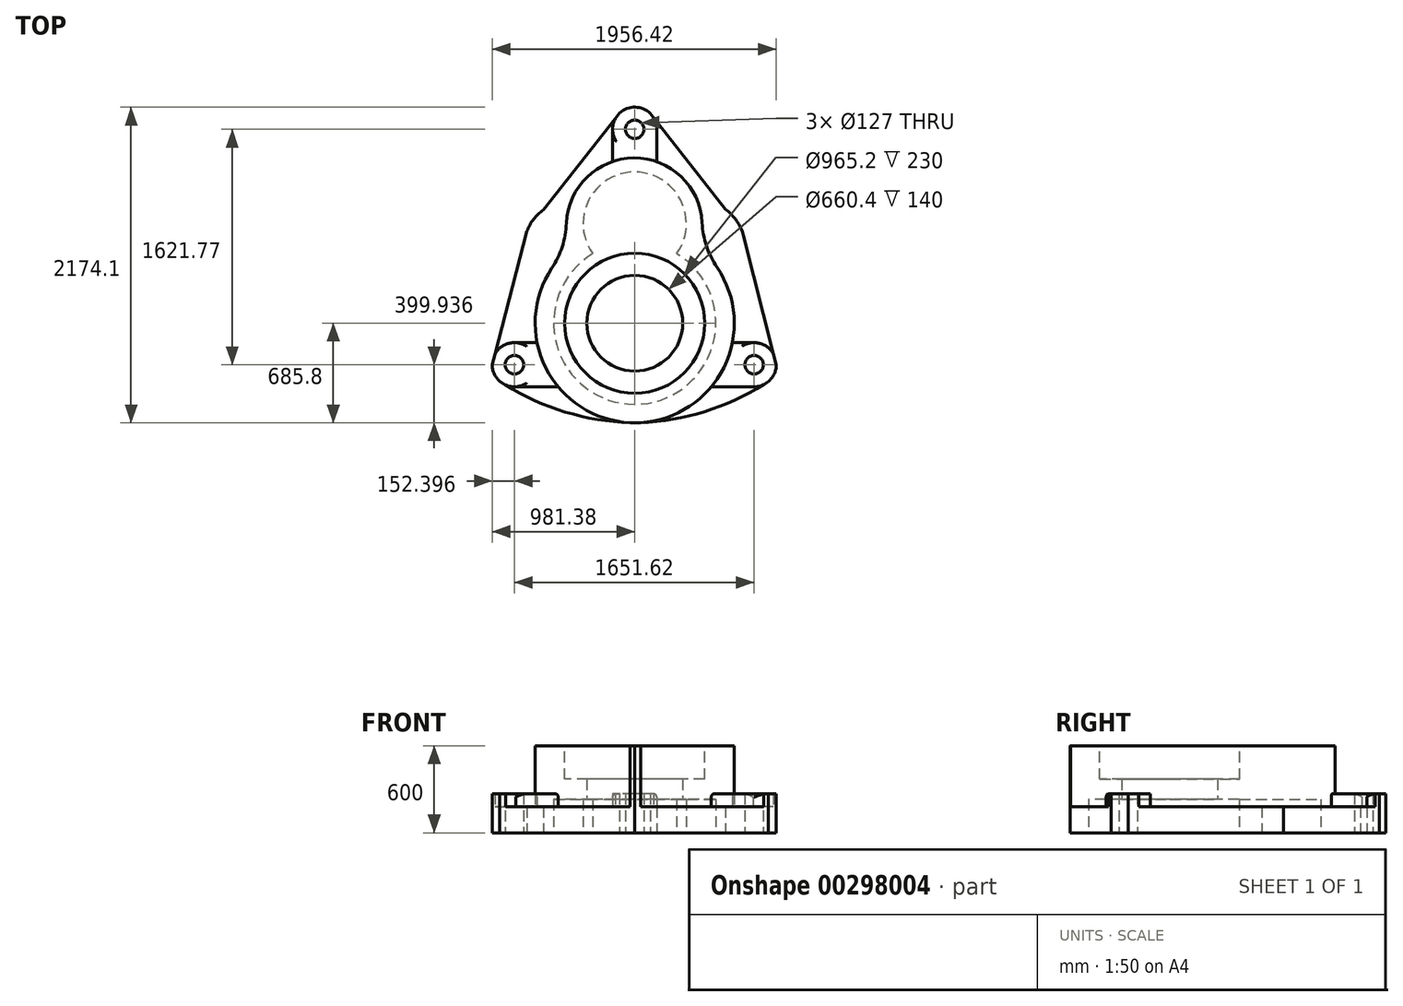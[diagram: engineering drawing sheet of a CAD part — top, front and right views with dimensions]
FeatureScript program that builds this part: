
annotation { "Feature Type Name" : "Feature", "Feature Type Description" : "" }
export const myFeature = defineFeature(function(context is Context, id is Id, definition is map)
    precondition{}
    {
        {
            var Q0;
            Q0=qCreatedBy(makeId("Top.planeOp"),FACE);
            var sketch = newSketch(context, id + "F0", { "sketchPlane" : qUnion([Q0])});
            skArc(sketch, "E0", {"start": v(-446.41, 520.61) * mm, "mid": v(3.07, -685.8) * mm, "end": v(441.73, 524.6) * mm});
            skCircle(sketch, "E1", {"center": v(0, 0) * mm, "radius": 330.2 * mm});
            skCircle(sketch, "E2", {"center": v(0, 0) * mm, "radius": 558.8 * mm});
            skCircle(sketch, "E3", {"center": v(-828.98, -285.86) * mm, "radius": 152.4 * mm});
            skCircle(sketch, "E4", {"center": v(822.64, -285.7) * mm, "radius": 152.4 * mm});
            skCircle(sketch, "E5", {"center": v(-828.98, -285.86) * mm, "radius": 63.5 * mm});
            skCircle(sketch, "E6", {"center": v(822.64, -285.7) * mm, "radius": 63.5 * mm});
            skLineSegment(sketch, "E7", {"start": v(-819.33, -437.96) * mm, "end": v(-527.72, -437.98) * mm});
            skLineSegment(sketch, "E8", {"start": v(-828.61, -133.46) * mm, "end": v(-672.69, -133.46) * mm});
            skLineSegment(sketch, "E9.trimOffspring", {"start": v(672.69, -133.46) * mm, "end": v(815.7, -133.46) * mm});
            skLineSegment(sketch, "E10.trimOffspring", {"start": v(527.64, -438.08) * mm, "end": v(822.62, -438.1) * mm});
            skCircle(sketch, "E11", {"center": v(0, 685.8) * mm, "radius": 355.6 * mm});
            skArc(sketch, "E12.trimOffspring", {"start": v(441.73, 524.6) * mm, "mid": v(-5.1, 1138.5) * mm, "end": v(-446.41, 520.61) * mm});
            skPoint(sketch, "E13.centerSnap0", {"position": v(-5.1, 1138.5) * mm});
            skArc(sketch, "E14", {"start": v(-132.99, 1410.33) * mm, "mid": v(2.72, 1183.53) * mm, "end": v(130.25, 1415.03) * mm});
            skLineSegment(sketch, "E15", {"start": v(150.95, 1356.87) * mm, "end": v(150.95, 1112.47) * mm});
            skLineSegment(sketch, "E16", {"start": v(-151.85, 1322.98) * mm, "end": v(-151.85, 1114.21) * mm});
            skCircle(sketch, "E17", {"center": v(0, 1335.9) * mm, "radius": 63.5 * mm});
            skLineSegment(sketch, "E18", {"start": v(-981.36, -283) * mm, "end": v(-981.36, -283) * mm});
            skArc(sketch, "E19", {"start": v(749.46, 602.73) * mm, "mid": v(702.96, 705.05) * mm, "end": v(623.72, 784.76) * mm});
            skArc(sketch, "E20", {"start": v(-628.54, 780.68) * mm, "mid": v(-717.12, 686.52) * mm, "end": v(-760.82, 564.85) * mm});
            skPoint(sketch, "E21.start.orphan", {"position": v(975.04, -285.7) * mm});
            skLineSegment(sketch, "E22", {"start": v(-981.36, -283) * mm, "end": v(-742.52, 635.17) * mm});
            skLineSegment(sketch, "E23", {"start": v(975.04, -285.7) * mm, "end": v(741.57, 633.83) * mm});
            skPoint(sketch, "E23.endSnap0", {"position": v(741.57, 629.01) * mm});
            skLineSegment(sketch, "E24", {"start": v(741.57, 633.83) * mm, "end": v(738.26, 638.07) * mm});
            skPoint(sketch, "E25.start.orphan", {"position": v(0, -685.8) * mm});
            skArc(sketch, "E26", {"start": v(-929.9, -400.07) * mm, "mid": v(-485.35, -609.35) * mm, "end": v(0, -685.8) * mm});
            skArc(sketch, "E27", {"start": v(0, -685.8) * mm, "mid": v(479.78, -609.45) * mm, "end": v(919.67, -403.23) * mm});
            skCircle(sketch, "E28", {"center": v(0, 0) * mm, "radius": 482.6 * mm});
            skArc(sketch, "E29.trimOffspring", {"start": v(343.44, 593.6) * mm, "mid": v(0, 685.8) * mm, "end": v(-343.44, 593.6) * mm});
            skLineSegment(sketch, "E30", {"start": v(130.25, 1415.03) * mm, "end": v(108.06, 1443.36) * mm});
            skLineSegment(sketch, "E31", {"start": v(-132.99, 1410.33) * mm, "end": v(-103.6, 1447.67) * mm});
            skArc(sketch, "E32.trimOffspring", {"start": v(108.06, 1443.36) * mm, "mid": v(3.1, 1488.27) * mm, "end": v(-103.6, 1447.67) * mm});
            skPoint(sketch, "E33", {"position": v(-110.4, 1439.03) * mm});
            skLineSegment(sketch, "E34", {"start": v(-628.54, 780.68) * mm, "end": v(-110.4, 1439.03) * mm});
            skPoint(sketch, "E35", {"position": v(111.45, 1439.03) * mm});
            skLineSegment(sketch, "E36", {"start": v(623.72, 784.76) * mm, "end": v(111.45, 1439.03) * mm});
            skSolve(sketch);
        }
        {
            var Q0;
            {var subQ6=sQuery(id+"F0.wireOp",EDGE,"E0");var subQ9=sQuery(id+"F0.wireOp",EDGE,"E12.trimOffspring");var subQ11=makeQuery(id+"F0.imprint","INTERSECT",VERTEX,{"disambiguationData":[OD(0.0)],"derivedFrom":[subQ6,subQ9]});Q0=makeQuery(id+"F0.imprint","IMPRINT",FACE,{"disambiguationData":[TD([[makeQuery(id+"F0.imprint","IMPRINT",EDGE,{"disambiguationData":[TD([[subQ11,-1.0]])],"derivedFrom":subQ6}),1.0]])]});}
            var Q1;
            {var subQ0=sQuery(id+"F0.wireOp",EDGE,"E29.trimOffspring");Q1=makeQuery(id+"F0.imprint","IMPRINT",FACE,{"disambiguationData":[TD([[makeQuery(id+"F0.imprint","IMPRINT",EDGE,{"derivedFrom":subQ0}),-1.0]])]});}
            var Q2;
            {var subQ4=sQuery(id+"F0.wireOp",EDGE,"E29.trimOffspring");Q2=makeQuery(id+"F0.imprint","IMPRINT",FACE,{"disambiguationData":[TD([[makeQuery(id+"F0.imprint","IMPRINT",EDGE,{"derivedFrom":subQ4}),1.0]])]});}
            var Q3;
            {var subQ0=sQuery(id+"F0.wireOp",EDGE,"E11");var subQ1=sQuery(id+"F0.wireOp",EDGE,"E2");var subQ2=makeQuery(id+"F0.imprint","INTERSECT",VERTEX,{"disambiguationData":[OD(0.0)],"derivedFrom":[subQ1,subQ0]});Q3=makeQuery(id+"F0.imprint","IMPRINT",FACE,{"disambiguationData":[TD([[makeQuery(id+"F0.imprint","IMPRINT",EDGE,{"disambiguationData":[TD([[subQ2,1.0]])],"derivedFrom":subQ1}),1.0]])]});}
            var Q4;
            {var subQ0=sQuery(id+"F0.wireOp",EDGE,"E11");var subQ1=makeQuery(id+"F0.imprint","INTERSECT",VERTEX,{"derivedFrom":[sQuery(id+"F0.wireOp",EDGE,"E1"),subQ0]});Q4=makeQuery(id+"F0.imprint","IMPRINT",FACE,{"disambiguationData":[TD([[makeQuery(id+"F0.imprint","IMPRINT",EDGE,{"disambiguationData":[TD([[subQ1,1.0]])],"derivedFrom":subQ0}),1.0]])]});}
            var Q5;
            {var subQ0=sQuery(id+"F0.wireOp",EDGE,"E11");var subQ1=sQuery(id+"F0.wireOp",EDGE,"E2");var subQ2=makeQuery(id+"F0.imprint","INTERSECT",VERTEX,{"disambiguationData":[OD(0.0)],"derivedFrom":[subQ1,subQ0]});Q5=makeQuery(id+"F0.imprint","IMPRINT",FACE,{"disambiguationData":[TD([[makeQuery(id+"F0.imprint","IMPRINT",EDGE,{"disambiguationData":[TD([[subQ2,-1.0]])],"derivedFrom":subQ1}),1.0]])]});}
            var Q6;
            Q6=makeQuery(id+"F0.imprint","IMPRINT",FACE,{"disambiguationData":[TD([[makeQuery(id+"F0.imprint","IMPRINT",EDGE,{"derivedFrom":sQuery(id+"F0.wireOp",EDGE,"E1")}),1.0]])]});
            var Q7;
            {var subQ0=sQuery(id+"F0.wireOp",EDGE,"E1");Q7=makeQuery(id+"F0.imprint","IMPRINT",FACE,{"disambiguationData":[TD([[makeQuery(id+"F0.imprint","IMPRINT",EDGE,{"derivedFrom":subQ0}),-1.0]])]});}
            extrude(context, id + "F1", {"entities" : qUnion([Q0, Q1, Q2, Q3, Q4, Q5, Q6, Q7]), "depth" : 600 * mm});
        }
        {
            var Q0;
            {var subQ0=sQuery(id+"F0.wireOp",EDGE,"E12.trimOffspring");var subQ1=sQuery(id+"F0.wireOp",EDGE,"E0");Q0=makeQuery(id+"F1.opExtrude","SWEPT_EDGE",EDGE,{"disambiguationData":[OSD([subQ1,subQ0]),TDD([makeQuery(id+"F0.imprint","INTERSECT",VERTEX,{"disambiguationData":[OD(0.0)],"derivedFrom":[subQ1,subQ0]})])]});}
            var Q1;
            {var subQ0=sQuery(id+"F0.wireOp",EDGE,"E12.trimOffspring");var subQ1=sQuery(id+"F0.wireOp",EDGE,"E0");Q1=makeQuery(id+"F1.opExtrude","SWEPT_EDGE",EDGE,{"disambiguationData":[OSD([subQ1,subQ0]),TDD([makeQuery(id+"F0.imprint","INTERSECT",VERTEX,{"disambiguationData":[OD(1.0)],"derivedFrom":[subQ1,subQ0]})])]});}
            fillet(context, id + "F2", {"entities" : qUnion([Q0, Q1]), "radius" : 600 * mm, "tangentPropagation" : true, "allowEdgeOverflow" : false});
        }
        {
            var Q0;
            {var subQ3=sQuery(id+"F0.wireOp",EDGE,"E16");Q0=makeQuery(id+"F0.imprint","IMPRINT",FACE,{"disambiguationData":[TD([[makeQuery(id+"F0.imprint","IMPRINT",EDGE,{"derivedFrom":subQ3}),1.0]])]});}
            var Q1;
            Q1=makeQuery(id+"F0.imprint","IMPRINT",FACE,{"disambiguationData":[TD([[makeQuery(id+"F0.imprint","IMPRINT",EDGE,{"derivedFrom":sQuery(id+"F0.wireOp",EDGE,"E17")}),-1.0]])]});
            var Q2;
            Q2=makeQuery(id+"F0.imprint","IMPRINT",FACE,{"disambiguationData":[TD([[makeQuery(id+"F0.imprint","IMPRINT",EDGE,{"derivedFrom":sQuery(id+"F0.wireOp",EDGE,"E6")}),-1.0]])]});
            var Q3;
            {var subQ0=sQuery(id+"F0.wireOp",EDGE,"E9.trimOffspring");Q3=makeQuery(id+"F0.imprint","IMPRINT",FACE,{"disambiguationData":[TD([[makeQuery(id+"F0.imprint","IMPRINT",EDGE,{"derivedFrom":subQ0}),-1.0]])]});}
            var Q4;
            {var subQ0=sQuery(id+"F0.wireOp",EDGE,"E7");Q4=makeQuery(id+"F0.imprint","IMPRINT",FACE,{"disambiguationData":[TD([[makeQuery(id+"F0.imprint","IMPRINT",EDGE,{"derivedFrom":subQ0}),1.0]])]});}
            var Q5;
            Q5=makeQuery(id+"F0.imprint","IMPRINT",FACE,{"disambiguationData":[TD([[makeQuery(id+"F0.imprint","IMPRINT",EDGE,{"derivedFrom":sQuery(id+"F0.wireOp",EDGE,"E5")}),-1.0]])]});
            extrude(context, id + "F3", {"entities" : qUnion([Q0, Q1, Q2, Q3, Q4, Q5]), "operationType" : NewBodyOperationType.ADD, "depth" : 270 * mm});
        }
        {
            var Q0;
            {var subQ4=sQuery(id+"F0.wireOp",EDGE,"E8");Q0=makeQuery(id+"F0.imprint","IMPRINT",FACE,{"disambiguationData":[TD([[makeQuery(id+"F0.imprint","IMPRINT",EDGE,{"derivedFrom":subQ4}),1.0]])]});}
            var Q1;
            {var subQ13=sQuery(id+"F0.wireOp",EDGE,"E9.trimOffspring");Q1=makeQuery(id+"F0.imprint","IMPRINT",FACE,{"disambiguationData":[TD([[makeQuery(id+"F0.imprint","IMPRINT",EDGE,{"derivedFrom":subQ13}),1.0]])]});}
            var Q2;
            {var subQ0=sQuery(id+"F0.wireOp",EDGE,"E10.trimOffspring");Q2=makeQuery(id+"F0.imprint","IMPRINT",FACE,{"disambiguationData":[TD([[makeQuery(id+"F0.imprint","IMPRINT",EDGE,{"derivedFrom":subQ0}),-1.0]])]});}
            var Q3;
            {var subQ0=sQuery(id+"F0.wireOp",EDGE,"E7");Q3=makeQuery(id+"F0.imprint","IMPRINT",FACE,{"disambiguationData":[TD([[makeQuery(id+"F0.imprint","IMPRINT",EDGE,{"derivedFrom":subQ0}),-1.0]])]});}
            extrude(context, id + "F4", {"entities" : qUnion([Q0, Q1, Q2, Q3]), "operationType" : NewBodyOperationType.ADD, "depth" : 180 * mm});
        }
        {
            var Q0;
            {var subQ0=sQuery(id+"F0.wireOp",EDGE,"E29.trimOffspring");Q0=makeQuery(id+"F0.imprint","IMPRINT",FACE,{"disambiguationData":[TD([[makeQuery(id+"F0.imprint","IMPRINT",EDGE,{"derivedFrom":subQ0}),-1.0]])]});}
            var Q1;
            {var subQ4=sQuery(id+"F0.wireOp",EDGE,"E29.trimOffspring");Q1=makeQuery(id+"F0.imprint","IMPRINT",FACE,{"disambiguationData":[TD([[makeQuery(id+"F0.imprint","IMPRINT",EDGE,{"derivedFrom":subQ4}),1.0]])]});}
            var Q2;
            {var subQ0=sQuery(id+"F0.wireOp",EDGE,"E11");var subQ1=sQuery(id+"F0.wireOp",EDGE,"E2");var subQ2=makeQuery(id+"F0.imprint","INTERSECT",VERTEX,{"disambiguationData":[OD(0.0)],"derivedFrom":[subQ1,subQ0]});Q2=makeQuery(id+"F0.imprint","IMPRINT",FACE,{"disambiguationData":[TD([[makeQuery(id+"F0.imprint","IMPRINT",EDGE,{"disambiguationData":[TD([[subQ2,1.0]])],"derivedFrom":subQ1}),1.0]])]});}
            var Q3;
            {var subQ0=sQuery(id+"F0.wireOp",EDGE,"E11");var subQ1=sQuery(id+"F0.wireOp",EDGE,"E2");var subQ2=makeQuery(id+"F0.imprint","INTERSECT",VERTEX,{"disambiguationData":[OD(0.0)],"derivedFrom":[subQ1,subQ0]});Q3=makeQuery(id+"F0.imprint","IMPRINT",FACE,{"disambiguationData":[TD([[makeQuery(id+"F0.imprint","IMPRINT",EDGE,{"disambiguationData":[TD([[subQ2,-1.0]])],"derivedFrom":subQ1}),1.0]])]});}
            var Q4;
            {var subQ0=sQuery(id+"F0.wireOp",EDGE,"E11");var subQ1=makeQuery(id+"F0.imprint","INTERSECT",VERTEX,{"derivedFrom":[sQuery(id+"F0.wireOp",EDGE,"E1"),subQ0]});Q4=makeQuery(id+"F0.imprint","IMPRINT",FACE,{"disambiguationData":[TD([[makeQuery(id+"F0.imprint","IMPRINT",EDGE,{"disambiguationData":[TD([[subQ1,1.0]])],"derivedFrom":subQ0}),1.0]])]});}
            var Q5;
            {var subQ0=sQuery(id+"F0.wireOp",EDGE,"E1");Q5=makeQuery(id+"F0.imprint","IMPRINT",FACE,{"disambiguationData":[TD([[makeQuery(id+"F0.imprint","IMPRINT",EDGE,{"derivedFrom":subQ0}),-1.0]])]});}
            var Q6;
            Q6=makeQuery(id+"F0.imprint","IMPRINT",FACE,{"disambiguationData":[TD([[makeQuery(id+"F0.imprint","IMPRINT",EDGE,{"derivedFrom":sQuery(id+"F0.wireOp",EDGE,"E1")}),1.0]])]});
            extrude(context, id + "F5", {"entities" : qUnion([Q0, Q1, Q2, Q3, Q4, Q5, Q6]), "operationType" : NewBodyOperationType.REMOVE, "depth" : 230 * mm});
        }
        {
            var Q0;
            Q0=makeQuery(id+"F1.opExtrude","CAP_FACE",FACE,{"disambiguationData":[OSD([sQuery(id+"F0.wireOp",EDGE,"E0"),sQuery(id+"F0.wireOp",EDGE,"E12.trimOffspring"),sQuery(id+"F0.wireOp",EDGE,"E26"),sQuery(id+"F0.wireOp",EDGE,"E27")])],"isStart":false});
            var sketch = newSketch(context, id + "F6", { "sketchPlane" : qUnion([Q0])});
            skCircle(sketch, "E37.0", {"center": v(0, 0) * mm, "radius": 482.6 * mm});
            skSolve(sketch);
        }
        {
            var Q0;
            Q0 = qSketchRegion(id + "F6", true);
            extrude(context, id + "F7", {"entities" : qUnion([Q0]), "operationType" : NewBodyOperationType.REMOVE, "oppositeDirection" : true, "depth" : 230 * mm});
        }
        {
            var Q0;
            Q0=makeQuery(id+"F0.imprint","IMPRINT",FACE,{"disambiguationData":[TD([[makeQuery(id+"F0.imprint","IMPRINT",EDGE,{"derivedFrom":sQuery(id+"F0.wireOp",EDGE,"E1")}),1.0]])]});
            extrude(context, id + "F8", {"entities" : qUnion([Q0]), "operationType" : NewBodyOperationType.REMOVE, "endBound" : BoundingType.THROUGH_ALL, "depth" : 25 * mm});
        }
        {
            var Q0;
            Q0=makeQuery(id+"F3.opExtrude","CAP_EDGE",EDGE,{"disambiguationData":[OSD([sQuery(id+"F0.wireOp",EDGE,"E15")])],"isStart":false});
            var Q1;
            Q1=makeQuery(id+"F3.opExtrude","CAP_EDGE",EDGE,{"disambiguationData":[OSD([sQuery(id+"F0.wireOp",EDGE,"E16")])],"isStart":false});
            var Q2;
            Q2=makeQuery(id+"F3.opExtrude","CAP_EDGE",EDGE,{"disambiguationData":[OSD([sQuery(id+"F0.wireOp",EDGE,"E7")])],"isStart":false});
            var Q3;
            Q3=makeQuery(id+"F3.opExtrude","CAP_EDGE",EDGE,{"disambiguationData":[OSD([sQuery(id+"F0.wireOp",EDGE,"E10.trimOffspring")])],"isStart":false});
            var Q4;
            Q4=makeQuery(id+"F3.opExtrude","CAP_EDGE",EDGE,{"disambiguationData":[OSD([sQuery(id+"F0.wireOp",EDGE,"E9.trimOffspring")])],"isStart":false});
            var Q5;
            Q5=makeQuery(id+"F3.opExtrude","CAP_EDGE",EDGE,{"disambiguationData":[OSD([sQuery(id+"F0.wireOp",EDGE,"E8")])],"isStart":false});
            fillet(context, id + "F9", {"entities" : qUnion([Q0, Q1, Q2, Q3, Q4, Q5]), "radius" : 24.14 * mm, "tangentPropagation" : true, "allowEdgeOverflow" : false});
        }
    });
